# Revit family: Elbow-MxF-B-PressXL-Water-Gas-Conex-65-100mm
name_source: partatom
category: Pipe Fittings
units: mm (PartAtom-declared; Revit-internal decimal feet)

## family parameters
Always vertical = Yes
Cut with Voids When Loaded = No
OmniClass Number = 23.60.30.11.14
OmniClass Title = Pipework Fittings
Part Type = Elbow
Round Connector Dimension = Use Diameter
Shared = No
Work Plane-Based = No

## types (2) — shared parameters
Assembly Code = D2090800
ConnectorTolerance = 2.00°
Description = >B< Press XL has only two internal parts, the grip ring and the seal. Both parts have an internal diameter larger than the tube, which allows for easy tube insertion and pre press leak indication.
K Coefficient Table = Regular 45, 90 and 180 Elbow
Lookup Table Name = Elbow-MxF-B-PressXL-Water-Gas-Conex-65-100mm
Loss Method = K Coefficient from Table
Manufacturer = Conex | Bänninger
Material = Copper
Model = Elbow - MxF 45° & 90°
Model Specification = BMA
Model Version = 2015
ModifiedIssue_ANZRS = 20161221.54 $
NATSPECWorkSection = TBC
OmniclassProducts = TBC
Type Comments = TBC
URL = http://www.conexbanninger.com.au
Uniformat IIElements = TBC

## per-type parameters (varying)
| type | WorkingFluidSelector |
| Gas | 1 |
| Water | 2 |

## geometry (parser evidence)
native form markers: Sweep x3
no freeform markers — native parametric forms only
